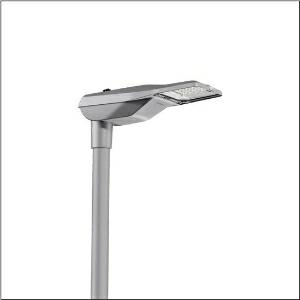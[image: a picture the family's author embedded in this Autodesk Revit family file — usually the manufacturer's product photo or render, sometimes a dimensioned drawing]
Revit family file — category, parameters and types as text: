
# Revit family: streetlight_sl_21_micro___st0_8a_5xe1c43s08db_42f9
name_source: partatom
category: Lighting Fixtures
units: mm (PartAtom-declared; Revit-internal decimal feet)

## family parameters
Cut with Voids When Loaded = No
Host = Face
Light Source = No
Part Type = Normal
Room Calculation Point = No
Round Connector Dimension = Use Diameter
Shared = No

## types (1)
- --- (1 x LED, 5320 lm, 39.1 W, 4000K)
    Apparent Load = 39 VA
    CIE Flux Codes = 38 75 97 100 100
    Color Rendering = 70
    Color Temperature = 4000K
    Default Elevation = 1800 mm
    Description = Streetlight SL 21 micro, mast luminaire, primary light control with lens, of PMMA, primary optical cover: cover, of toughened safety glass, transparent, light distribution: ST0.8a, light emission: direct distribution, primary light characteristic: asymmetric, installation type: side-entry, post-top, LED, High Power LED, rated luminous flux: 5.320lm, luminous efficacy: 136lm/W, light colour: 740, colour temperature: 4000K, control gear: D4i, control: flexible luminous flux parameterisation, time-dependent luminous flux control, constant luminous flux control, overheat protection, pre-setting: logarithmic dimming characteristic, mains connection: 220..240V, AC, 50/60Hz, start of lifetime: 39W, end of service life: 41W, reduction: 18W, luminaire housing, of diecast aluminium, powder-coated, SITECO metallic grey (DB 702S), corrosivity category C5 high according to DIN EN ISO 12944, please order mast flange separately, inclination adjustable: 0°, 5°, 10°, 15°, sealing non-destructively replaceable, multi-level sealing system, length: 528mm, width: 235mm, height: 110mm, mast flange for spigot size: 42mm (side-entry): 5XC10008XM4, 60/48mm (side-entry/post-top): 5XC10108XM2, 76/60mm (side-entry/post-top): 5XC10108XM1, Smart Interface above, protection rating (complete): IP66, insulation class (complete): insulation class II (safety insulation), certification: CE, ENEC, ENEC+, VDE, impact resistance: IK10, permissible operating ambient temperature for outdoor applications: -40..+50°C, standard-compliant lighting for roads and squares, packaging unit: 1 piece

Light Distribution: ST0.8a
    Height = 110 mm
    Lamp = 1 x LED
    Lamp Light Flux = 5320 lm
    Lamp Power = 39.1 W
    Lamp count = 1
    Length = 528 mm
    Luminous efficacy = 136 lm/W
    Manufacturer = Siteco
    ModVariant = No
    Model = 5XE1C43S08DB
    Number of Poles = 1
    OnlyDefault = Yes
    Power Factor = 1
    Product Name = Streetlight SL 21 micro | ST0.8a
    Product group = mast luminaire | pylon top
    ProductGroupID = 6100
    Protection Class = Protection class II
    Protection Degree = IP 66
    RLX_Detail_Level = 1
    RLX_Emergency_Light_Flux = 0 lm
    RLX_Emergency_Type = 0
    RLX_Emergency_Type_DB = No
    RlxData = <blob elided: 98289 chars, md5=0b3f8579>
    Socket = socket
    Standby Power = 0 W
    System Light Flux = 5320 lm
    System Power = 39 W
    Type Comments = factory setting: luminous flux: 100 % | dim-lin: 254 | 765 mA
    Type Image = l_1277292.jpg
    URL = http://relux.com
    VarID = @adj_153881
    Voltage = 0 V
    Weight = 0.00 kg
    Width = 235 mm

## geometry (parser evidence)
native form markers: Blend x4, Sweep x10
no freeform markers — native parametric forms only
